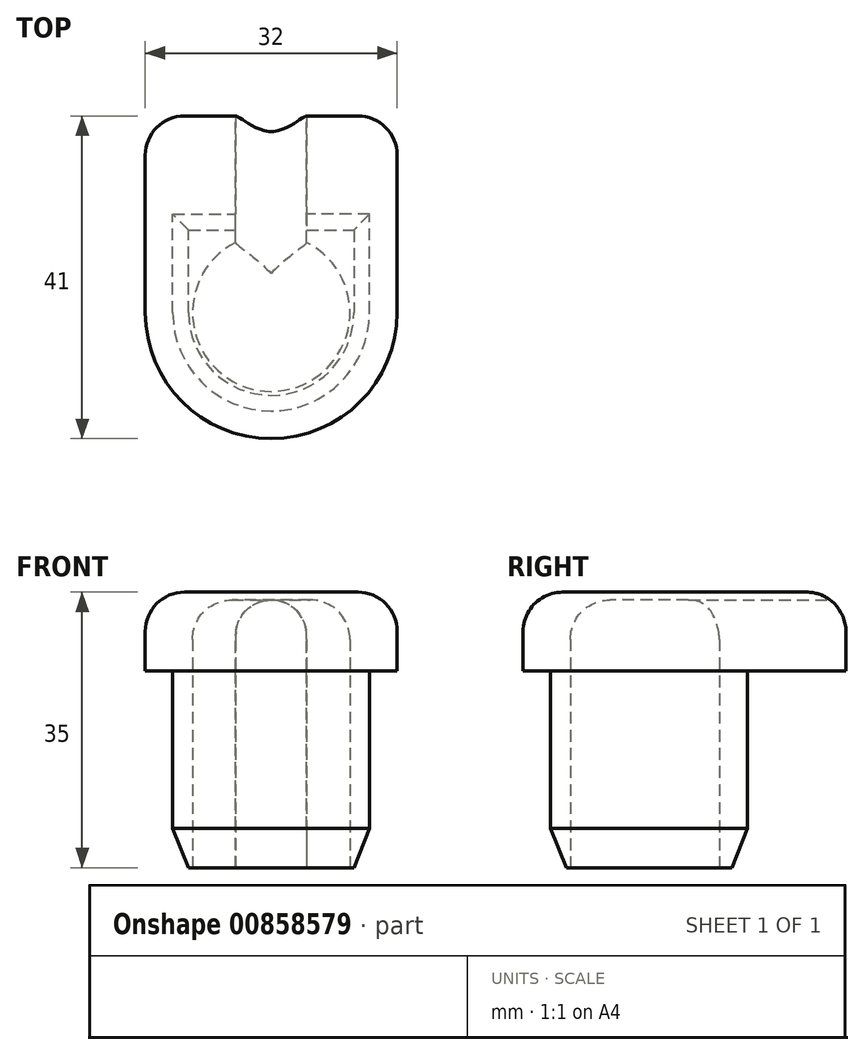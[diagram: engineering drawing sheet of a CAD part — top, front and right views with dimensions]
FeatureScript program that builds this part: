
annotation { "Feature Type Name" : "Feature", "Feature Type Description" : "" }
export const myFeature = defineFeature(function(context is Context, id is Id, definition is map)
    precondition{}
    {
        {
            var Q0;
            Q0=qCreatedBy(makeId("Top.planeOp"),FACE);
            var sketch = newSketch(context, id + "F0", { "sketchPlane" : qUnion([Q0])});
            skLineSegment(sketch, "E0", {"start": v(0, 12.5) * mm, "end": v(12.5, 12.5) * mm});
            skArc(sketch, "E1", {"start": v(-12.5, 0) * mm, "mid": v(0, -12.5) * mm, "end": v(12.5, 0) * mm});
            skLineSegment(sketch, "E2", {"start": v(12.5, 0) * mm, "end": v(12.5, 12.5) * mm});
            skLineSegment(sketch, "E3.MirrorCS", {"start": v(0, 12.5) * mm, "end": v(-12.5, 12.5) * mm});
            skLineSegment(sketch, "E4.MirrorCS", {"start": v(-12.5, 0) * mm, "end": v(-12.5, 12.5) * mm});
            skSolve(sketch);
        }
        {
            var Q0;
            Q0 = qSketchRegion(id + "F0", true);
            extrude(context, id + "F1", {"entities" : qUnion([Q0]), "depth" : 25 * mm, "offsetDistance" : 25 * mm});
        }
        {
            var Q0;
            Q0=makeQuery(id+"F1.opExtrude","CAP_FACE",FACE,{"disambiguationData":[OSD([sQuery(id+"F0.wireOp",EDGE,"E0"),sQuery(id+"F0.wireOp",EDGE,"E1"),sQuery(id+"F0.wireOp",EDGE,"E2"),sQuery(id+"F0.wireOp",EDGE,"E3.MirrorCS"),sQuery(id+"F0.wireOp",EDGE,"E4.MirrorCS")])],"isStart":false});
            var sketch = newSketch(context, id + "F2", { "sketchPlane" : qUnion([Q0])});
            skLineSegment(sketch, "E5", {"start": v(0, 25) * mm, "end": v(16, 25) * mm});
            skLineSegment(sketch, "E6", {"start": v(16, 25) * mm, "end": v(16, 0) * mm});
            skLineSegment(sketch, "E7.MirrorCS", {"start": v(0, 25) * mm, "end": v(-16, 25) * mm});
            skLineSegment(sketch, "E8.MirrorCS", {"start": v(-16, 25) * mm, "end": v(-16, 0) * mm});
            skArc(sketch, "E9", {"start": v(-16, 0) * mm, "mid": v(0, -16) * mm, "end": v(16, 0) * mm});
            skSolve(sketch);
        }
        {
            var Q0;
            Q0 = qSketchRegion(id + "F2", true);
            extrude(context, id + "F3", {"entities" : qUnion([Q0]), "operationType" : NewBodyOperationType.ADD, "depth" : 10 * mm, "offsetDistance" : 25 * mm});
        }
        {
            var Q0;
            Q0=makeQuery(id+"F1.opExtrude","CAP_FACE",FACE,{"disambiguationData":[OSD([sQuery(id+"F0.wireOp",EDGE,"E0"),sQuery(id+"F0.wireOp",EDGE,"E1"),sQuery(id+"F0.wireOp",EDGE,"E2"),sQuery(id+"F0.wireOp",EDGE,"E3.MirrorCS"),sQuery(id+"F0.wireOp",EDGE,"E4.MirrorCS")])],"isStart":true});
            var sketch = newSketch(context, id + "F4", { "sketchPlane" : qUnion([Q0])});
            skCircle(sketch, "E10", {"center": v(0, 0) * mm, "radius": 10 * mm});
            skSolve(sketch);
        }
        {
            var Q0;
            Q0 = qSketchRegion(id + "F4", true);
            extrude(context, id + "F5", {"entities" : qUnion([Q0]), "operationType" : NewBodyOperationType.REMOVE, "oppositeDirection" : true, "depth" : 34 * mm, "offsetDistance" : 25 * mm});
        }
        {
            var Q0;
            Q0=makeQuery(id+"F3.opExtrude","SWEPT_FACE",FACE,{"disambiguationData":[OSD([sQuery(id+"F2.wireOp",EDGE,"E5"),sQuery(id+"F2.wireOp",EDGE,"E7.MirrorCS")])]});
            var sketch = newSketch(context, id + "F6", { "sketchPlane" : qUnion([Q0])});
            skLineSegment(sketch, "E11", {"start": v(-4.5, 0) * mm, "end": v(-4.5, 29.5) * mm});
            skLineSegment(sketch, "E12.MirrorCS", {"start": v(4.5, 0) * mm, "end": v(4.5, 29.5) * mm});
            skArc(sketch, "E13", {"start": v(4.5, 29.5) * mm, "mid": v(0, 34) * mm, "end": v(-4.5, 29.5) * mm});
            skLineSegment(sketch, "E14", {"start": v(-4.5, 0) * mm, "end": v(4.5, 0) * mm});
            skSolve(sketch);
        }
        {
            var Q0;
            Q0 = qSketchRegion(id + "F6", true);
            extrude(context, id + "F7", {"entities" : qUnion([Q0]), "operationType" : NewBodyOperationType.REMOVE, "oppositeDirection" : true, "depth" : 25 * mm, "offsetDistance" : 25 * mm});
        }
        {
            var Q0;
            Q0=makeQuery(id+"F3.opExtrude","CAP_FACE",FACE,{"disambiguationData":[OSD([sQuery(id+"F2.wireOp",EDGE,"E5"),sQuery(id+"F2.wireOp",EDGE,"E6"),sQuery(id+"F2.wireOp",EDGE,"E7.MirrorCS"),sQuery(id+"F2.wireOp",EDGE,"E8.MirrorCS"),sQuery(id+"F2.wireOp",EDGE,"E9")])],"isStart":false});
            var Q1;
            Q1=makeQuery(id+"F5.boolean.opBoolean","COPY",FACE,{"derivedFrom":makeQuery(id+"F5.opExtrude","CAP_FACE",FACE,{"disambiguationData":[OSD([sQuery(id+"F4.wireOp",EDGE,"E10")])],"isStart":false})});
            fillet(context, id + "F8", {"entities" : qUnion([Q0, Q1]), "tangentPropagation" : true, "radius" : 5 * mm, "defaultsChanged" : false, "vertexSettings" : [], "allowEdgeOverflow" : false});
        }
        {
            var Q0;
            Q0=makeQuery(id+"F3.opExtrude","SWEPT_EDGE",EDGE,{"disambiguationData":[OSD([sQuery(id+"F2.wireOp",EDGE,"E5"),sQuery(id+"F2.wireOp",EDGE,"E6")])]});
            var Q1;
            Q1=makeQuery(id+"F3.opExtrude","SWEPT_EDGE",EDGE,{"disambiguationData":[OSD([sQuery(id+"F2.wireOp",EDGE,"E7.MirrorCS"),sQuery(id+"F2.wireOp",EDGE,"E8.MirrorCS")])]});
            fillet(context, id + "F9", {"entities" : qUnion([Q0, Q1]), "tangentPropagation" : true, "radius" : 5 * mm, "defaultsChanged" : false, "vertexSettings" : [], "allowEdgeOverflow" : false});
        }
        {
            var Q0;
            Q0=makeQuery(id+"F1.opExtrude","CAP_EDGE",EDGE,{"disambiguationData":[OSD([sQuery(id+"F0.wireOp",EDGE,"E2")])],"isStart":true});
            var Q1;
            {var subQ0=sQuery(id+"F0.wireOp",EDGE,"E3.MirrorCS");var subQ1=sQuery(id+"F0.wireOp",EDGE,"E2");var subQ2=sQuery(id+"F0.wireOp",EDGE,"E0");Q1=makeQuery(id+"F7.boolean.opBoolean","SPLIT",EDGE,{"disambiguationData":[TD([makeQuery(id+"F1.opExtrude","SWEPT_FACE",FACE,{"disambiguationData":[OSD([subQ1])]})])],"derivedFrom":makeQuery(id+"F1.opExtrude","CAP_EDGE",EDGE,{"disambiguationData":[OSD([subQ2,subQ0])],"isStart":true})});}
            var Q2;
            {var subQ0=sQuery(id+"F0.wireOp",EDGE,"E4.MirrorCS");var subQ1=sQuery(id+"F0.wireOp",EDGE,"E3.MirrorCS");var subQ2=sQuery(id+"F0.wireOp",EDGE,"E0");Q2=makeQuery(id+"F7.boolean.opBoolean","SPLIT",EDGE,{"disambiguationData":[TD([makeQuery(id+"F1.opExtrude","SWEPT_FACE",FACE,{"disambiguationData":[OSD([subQ0])]})])],"derivedFrom":makeQuery(id+"F1.opExtrude","CAP_EDGE",EDGE,{"disambiguationData":[OSD([subQ2,subQ1])],"isStart":true})});}
            chamfer(context, id + "F10", {"entities" : qUnion([Q0, Q1, Q2]), "chamferType" : ChamferType.TWO_OFFSETS, "width1" : 2 * mm, "oppositeDirection" : true, "width2" : 5 * mm, "tangentPropagation" : true});
        }
    });
